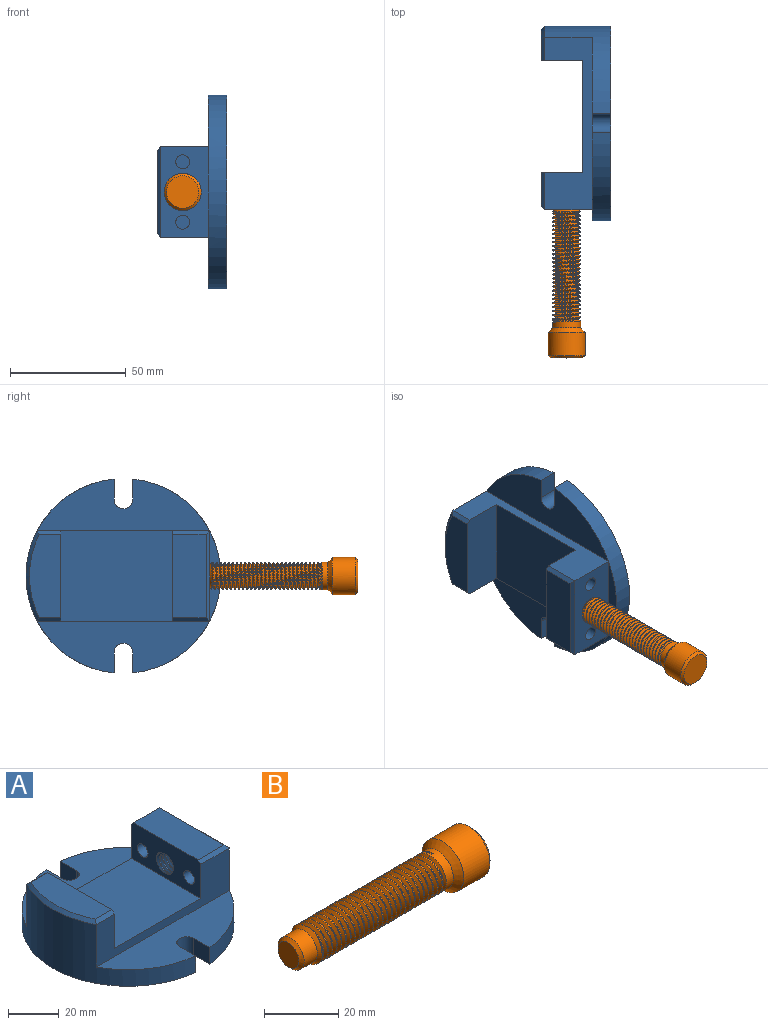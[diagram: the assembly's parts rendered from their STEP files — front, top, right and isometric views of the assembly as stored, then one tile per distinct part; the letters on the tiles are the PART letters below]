
ASSEMBLY  parts=2 mates=1
PART A: 32 faces, bbox 84.5x84.1x30.5 mm
  f0: plane 39.48x18.48mm, normal (-1,0,0), area 574.3mm2, adj f14,f15,f18,f19,f20,f21,f22,f23
  f1: plane 39.5x21mm, normal (1,0,0), area 674mm2, adj f4,f14,f15,f19,f20,f22,f23,f24
  f2: plane 74.4x22.31mm, normal (0,0,1), area 1097.3mm2, adj f6,f7,f8,f9,f10,f14
  f3: plane 74.4x22.31mm, normal (0,0,1), area 1097.3mm2, adj f5,f6,f10,f11,f12,f15
  f4: plane 39x4.8mm, normal (0,0,1), area 126.3mm2, adj f1,f6
  f5: plane 9.05x8mm, normal (-1,0,0), area 72.4mm2, adj f3,f6,f12,f13
  f6: cylinder r=42mm len=83.62mm, axis (0,0,1), area 991.6mm2, adj f2,f3,f4,f5,f7,f13
  f7: plane 9.05x8mm, normal (-1,0,0), area 72.4mm2, adj f2,f6,f8,f13
  f8: cylinder r=4mm len=8mm, axis (0,0,1), area 96.6mm2, adj f2,f7,f9,f13
  f9: plane 9.05x8mm, normal (1,0,0), area 72.4mm2, adj f2,f8,f10,f13
  f10: cylinder r=42mm len=83.62mm, axis (0,0,1), area 1823mm2, adj f2,f3,f9,f11,f13,f14,f15,f27
  f11: plane 9.05x8mm, normal (1,0,0), area 72.4mm2, adj f3,f10,f12,f13
  f12: cylinder r=4mm len=8mm, axis (0,0,1), area 96.6mm2, adj f3,f5,f11,f13
  f13: plane 84x83.62mm, normal (0,0,-1), area 5348.8mm2, adj f5,f6,f7,f8,f9,f10,f11,f12
  f14: plane 74.4x20.5mm, normal (0,1,0), area 729.9mm2, adj f0,f1,f2,f10,f16,f21,f28,f31
  f15: plane 74.4x20.5mm, normal (0,-1,0), area 729.9mm2, adj f0,f1,f3,f10,f16,f21,f26,f30
  f16: plane 39x18mm, normal (1,0,0), area 699.8mm2, adj f14,f15,f17,f21,f26,f28
  f17: plane 36x13.5mm, normal (0,0,1), area 436.5mm2, adj f16,f26,f27,f28
  f18: plane 36x14.5mm, normal (0,0,1), area 522mm2, adj f0,f29,f30,f31
  f19: cylinder r=3mm len=16mm, axis (1,0,0), area 301.6mm2, adj f0,f1
  f20: cylinder r=3mm len=16mm, axis (1,0,0), area 301.6mm2, adj f0,f1
  f21: plane 48.2x39mm, normal (0,0,1), area 1879.8mm2, adj f0,f14,f15,f16
  f22: bspline ~17.17x12mm, area 297.9mm2, adj f0,f1,f24,f25
  f23: bspline ~17.46x12mm, area 296.8mm2, adj f0,f1,f24,f25
  f24: bspline ~16.55x12.19mm, area 76.5mm2, adj f0,f1,f22,f23
  f25: cylinder r=4.25mm len=16mm, axis (-1,0,0), area 84.3mm2, adj f0,f1,f22,f23
  f26: plane 10.21x1.51mm, normal (0,-0.71,0.71), area 20.7mm2, adj f15,f16,f17,f27
  f27: cone r=40.5mm half-angle=45deg, axis (0,0,-1), area 82.6mm2, adj f10,f17,f26,f28
  f28: plane 10.21x1.51mm, normal (0,0.71,0.71), area 20.7mm2, adj f14,f16,f17,f27
  f29: plane 39x1.5mm, normal (0.71,0,0.71), area 79.5mm2, adj f1,f18,f30,f31
  f30: plane 16x1.5mm, normal (0,-0.71,0.71), area 32.4mm2, adj f0,f15,f18,f29
  f31: plane 16x1.5mm, normal (0,0.71,0.71), area 32.4mm2, adj f0,f14,f18,f29
PART B: 43 faces, bbox 70.5x16.5x16.5 mm
  f0: plane 8x8mm, normal (-1,0,0), area 50.3mm2, adj f33
  f1: plane 14x14mm, normal (1,0,0), area 153.9mm2, adj f34
  f2: cylinder r=8mm len=16mm, axis (-1,0,0), area 502.7mm2, adj f32,f34
  f3: cylinder r=6mm len=12mm, axis (-1,0,0), area 107.4mm2, adj f4,f32,f35,f36,f37,f40
  f4: cylinder r=6mm len=12mm, axis (-1,0,0), area 8.2mm2, adj f3,f5,f39,f40
  f5: cylinder r=6mm len=12mm, axis (-1,0,0), area 8.2mm2, adj f4,f6,f39,f40
  f6: cylinder r=6mm len=12mm, axis (-1,0,0), area 8.3mm2, adj f5,f7,f39,f40
  f7: cylinder r=6mm len=12mm, axis (-1,0,0), area 8.3mm2, adj f6,f8,f39,f40
  f8: cylinder r=6mm len=12mm, axis (-1,0,0), area 8.2mm2, adj f7,f9,f39,f40
  f9: cylinder r=6mm len=12mm, axis (-1,0,0), area 8.3mm2, adj f8,f10,f39,f40
  f10: cylinder r=6mm len=12mm, axis (-1,0,0), area 8.2mm2, adj f9,f11,f39,f40
  f11: cylinder r=6mm len=12mm, axis (-1,0,0), area 8.2mm2, adj f10,f12,f39,f40
  f12: cylinder r=6mm len=12mm, axis (-1,0,0), area 8.3mm2, adj f11,f13,f39,f40
  f13: cylinder r=6mm len=12mm, axis (-1,0,0), area 8.3mm2, adj f12,f14,f39,f40
  f14: cylinder r=6mm len=12mm, axis (-1,0,0), area 8.3mm2, adj f13,f15,f39,f40
  f15: cylinder r=6mm len=12mm, axis (-1,0,0), area 8.2mm2, adj f14,f16,f39,f40
  f16: cylinder r=6mm len=12mm, axis (-1,0,0), area 8.2mm2, adj f15,f17,f39,f40
  f17: cylinder r=6mm len=12mm, axis (-1,0,0), area 8.3mm2, adj f16,f18,f39,f40
  f18: cylinder r=6mm len=12mm, axis (-1,0,0), area 8.2mm2, adj f17,f19,f39,f40
  f19: cylinder r=6mm len=12mm, axis (-1,0,0), area 8.3mm2, adj f18,f20,f39,f40
  f20: cylinder r=6mm len=12mm, axis (-1,0,0), area 8.3mm2, adj f19,f21,f39,f40
  f21: cylinder r=6mm len=12mm, axis (-1,0,0), area 8.2mm2, adj f20,f22,f39,f40
  f22: cylinder r=6mm len=12mm, axis (-1,0,0), area 8.2mm2, adj f21,f23,f39,f40
  f23: cylinder r=6mm len=12mm, axis (-1,0,0), area 8.2mm2, adj f22,f24,f39,f40
  f24: cylinder r=6mm len=12mm, axis (-1,0,0), area 8.2mm2, adj f23,f25,f39,f40
  f25: cylinder r=6mm len=12mm, axis (-1,0,0), area 8.3mm2, adj f24,f26,f39,f40
  f26: cylinder r=6mm len=12mm, axis (-1,0,0), area 8.3mm2, adj f25,f27,f39,f40
  f27: cylinder r=6mm len=12mm, axis (-1,0,0), area 8.2mm2, adj f26,f28,f39,f40
  f28: cylinder r=6mm len=12mm, axis (-1,0,0), area 8.2mm2, adj f27,f29,f39,f40
  f29: cylinder r=6mm len=12mm, axis (-1,0,0), area 7.5mm2, adj f28,f31,f39,f40
  f30: cylinder r=5mm len=10mm, axis (-1,0,0), area 157.1mm2, adj f31,f33
  f31: cone r=5mm half-angle=45deg, axis (1,0,0), area 48.9mm2, adj f29,f30,f42
  f32: cone r=7mm half-angle=45deg, axis (1,0,0), area 124.4mm2, adj f2,f3
  f33: cone r=4mm half-angle=45deg, axis (1,0,0), area 40mm2, adj f0,f30
  f34: cone r=8mm half-angle=45deg, axis (-1,0,0), area 66.6mm2, adj f1,f2
  f35: plane 0.53x0.18mm, normal (0.01,1,0), area 0.1mm2, adj f3,f36,f37,f41
  f36: bspline ~13.36x12.97mm, area 21mm2, adj f3,f35,f39,f41
  f37: bspline ~13.36x12.97mm, area 21mm2, adj f3,f35,f40,f41
  f38: bspline ~47.1x11.67mm, area 405.4mm2, adj f39,f40,f41,f42
  f39: bspline ~46.63x13.86mm, area 993.4mm2, adj f4,f5,f6,f7,f8,f9,f10,f11
  f40: bspline ~47.8x13.86mm, area 1021.9mm2, adj f3,f4,f5,f6,f7,f8,f9,f10
  f41: bspline ~11.46x11.06mm, area 16.7mm2, adj f35,f36,f37,f38
  f42: plane 12.48x12.48mm, normal (1,0,0), area 19.3mm2, adj f31,f38,f39,f40
PLACE A rot(axis=(0.58,-0.58,-0.58),120deg) t=(83.83,104.63,56.07)mm
PLACE B rot(axis=(-0.58,0.58,-0.58),120deg) t=(72.83,-10.18,-36.32)mm
MATE revolute B.f2 <-> A.f25  axis (0,1,0) through (72.83,67.43,56.07)mm
